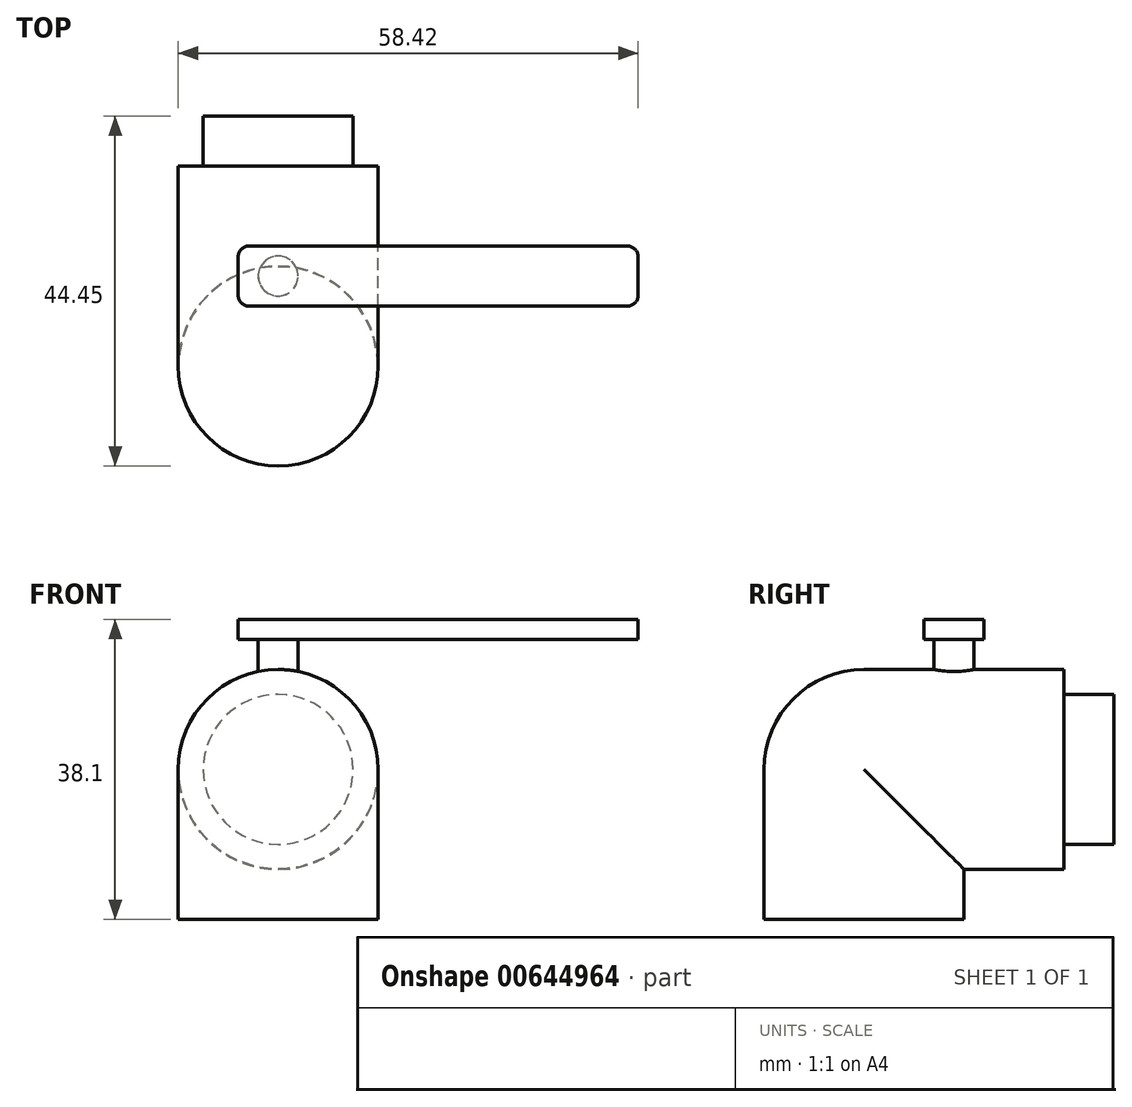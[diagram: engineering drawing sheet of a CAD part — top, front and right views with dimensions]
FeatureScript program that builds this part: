
annotation { "Feature Type Name" : "Feature", "Feature Type Description" : "" }
export const myFeature = defineFeature(function(context is Context, id is Id, definition is map)
    precondition{}
    {
        {
            var Q0;
            Q0=qCreatedBy(makeId("Front.planeOp"),FACE);
            var sketch = newSketch(context, id + "F0", { "sketchPlane" : qUnion([Q0])});
            skCircle(sketch, "E0", {"center": v(0, 0) * mm, "radius": 9.53 * mm});
            skSolve(sketch);
        }
        {
            var Q0;
            Q0 = qSketchRegion(id + "F0", true);
            extrude(context, id + "F1", {"entities" : qUnion([Q0]), "depth" : 6.35 * mm, "offsetDistance" : 25.4 * mm});
        }
        {
            var Q0;
            Q0=makeQuery(id+"F1.opExtrude","CAP_FACE",FACE,{"disambiguationData":[OSD([sQuery(id+"F0.wireOp",EDGE,"E0")])],"isStart":false});
            var sketch = newSketch(context, id + "F2", { "sketchPlane" : qUnion([Q0])});
            skCircle(sketch, "E1", {"center": v(0, 0) * mm, "radius": 12.7 * mm});
            skSolve(sketch);
        }
        {
            var Q0;
            Q0 = qSketchRegion(id + "F2", true);
            extrude(context, id + "F3", {"entities" : qUnion([Q0]), "operationType" : NewBodyOperationType.ADD, "depth" : 25.4 * mm, "offsetDistance" : 25.4 * mm});
        }
        {
            var Q0;
            Q0=qCreatedBy(makeId("Right.planeOp"),FACE);
            var sketch = newSketch(context, id + "F4", { "sketchPlane" : qUnion([Q0])});
            skLineSegment(sketch, "E2", {"start": v(-31.75, 0) * mm, "end": v(-31.75, 0) * mm});
            skArc(sketch, "E3", {"start": v(-31.75, 12.7) * mm, "mid": v(-40.73, 8.98) * mm, "end": v(-44.45, 0) * mm});
            skLineSegment(sketch, "E4", {"start": v(-44.45, 0) * mm, "end": v(-31.75, 0) * mm});
            skLineSegment(sketch, "E5", {"start": v(-31.75, 0) * mm, "end": v(-31.75, 12.7) * mm});
            skSolve(sketch);
        }
        {
            var Q0;
            Q0=makeQuery(id+"F4.imprint","IMPRINT",FACE,{"disambiguationData":[TD([[makeQuery(id+"F4.imprint","IMPRINT",EDGE,{"derivedFrom":sQuery(id+"F4.wireOp",EDGE,"E3")}),1.0]])]});
            var Q1;
            Q1=sQuery(id+"F4.wireOp",EDGE,"E5");
            revolve(context, id + "F5", {"operationType" : NewBodyOperationType.ADD, "entities" : qUnion([Q0]), "axis" : qUnion([Q1]), "revolveType" : RevolveType.FULL});
        }
        {
            var Q0;
            Q0=makeQuery(id+"F5.opRevolve","SWEPT_FACE",FACE,{"disambiguationData":[OSD([sQuery(id+"F4.wireOp",EDGE,"E4")])]});
            var sketch = newSketch(context, id + "F6", { "sketchPlane" : qUnion([Q0])});
            skCircle(sketch, "E6", {"center": v(0, 31.75) * mm, "radius": 12.7 * mm});
            skSolve(sketch);
        }
        {
            var Q0;
            Q0 = qSketchRegion(id + "F6", true);
            extrude(context, id + "F7", {"entities" : qUnion([Q0]), "operationType" : NewBodyOperationType.ADD, "depth" : 19.05 * mm, "offsetDistance" : 25.4 * mm});
        }
        {
            var Q0;
            Q0=qCreatedBy(makeId("Top.planeOp"),FACE);
            var sketch = newSketch(context, id + "F8", { "sketchPlane" : qUnion([Q0])});
            skCircle(sketch, "E7", {"center": v(0, -20.32) * mm, "radius": 2.54 * mm});
            skSolve(sketch);
        }
        {
            var Q0;
            Q0 = qSketchRegion(id + "F8", true);
            extrude(context, id + "F9", {"entities" : qUnion([Q0]), "operationType" : NewBodyOperationType.ADD, "depth" : 19.05 * mm, "offsetDistance" : 25.4 * mm});
        }
        {
            var Q0;
            Q0=makeQuery(id+"F9.opExtrude","CAP_FACE",FACE,{"disambiguationData":[OSD([sQuery(id+"F8.wireOp",EDGE,"E7")])],"isStart":false});
            var sketch = newSketch(context, id + "F10", { "sketchPlane" : qUnion([Q0])});
            skCircle(sketch, "E8", {"center": v(0, -20.32) * mm, "radius": 2.54 * mm});
            skLineSegment(sketch, "E9.bottom", {"start": v(44.36, -16.51) * mm, "end": v(-3.72, -16.51) * mm});
            skLineSegment(sketch, "E9.top", {"start": v(44.36, -24.13) * mm, "end": v(-3.72, -24.13) * mm});
            skLineSegment(sketch, "E9.left", {"start": v(45.72, -17.87) * mm, "end": v(45.72, -22.77) * mm});
            skLineSegment(sketch, "E9.right", {"start": v(-5.08, -17.87) * mm, "end": v(-5.08, -22.77) * mm});
            skPoint(sketch, "E10.visualSharp", {"position": v(-5.08, -16.51) * mm});
            skArc(sketch, "E10.filletArc", {"start": v(-3.72, -16.51) * mm, "mid": v(-4.68, -16.9) * mm, "end": v(-5.08, -17.87) * mm});
            skPoint(sketch, "E11.visualSharp", {"position": v(-5.08, -24.13) * mm});
            skArc(sketch, "E11.filletArc", {"start": v(-5.08, -22.77) * mm, "mid": v(-4.68, -23.73) * mm, "end": v(-3.72, -24.13) * mm});
            skPoint(sketch, "E12.visualSharp", {"position": v(45.72, -24.13) * mm});
            skArc(sketch, "E12.filletArc", {"start": v(44.36, -24.13) * mm, "mid": v(45.32, -23.73) * mm, "end": v(45.72, -22.77) * mm});
            skPoint(sketch, "E13.visualSharp", {"position": v(45.72, -16.5) * mm});
            skArc(sketch, "E13.filletArc", {"start": v(45.72, -17.87) * mm, "mid": v(45.32, -16.9) * mm, "end": v(44.36, -16.51) * mm});
            skSolve(sketch);
        }
        {
            var Q0;
            Q0=makeQuery(id+"F10.imprint","IMPRINT",FACE,{"disambiguationData":[TD([[makeQuery(id+"F10.imprint","IMPRINT",EDGE,{"derivedFrom":sQuery(id+"F10.wireOp",EDGE,"E8")}),-1.0]])]});
            extrude(context, id + "F11", {"entities" : qUnion([Q0]), "operationType" : NewBodyOperationType.ADD, "oppositeDirection" : true, "depth" : 2.54 * mm, "offsetDistance" : 25.4 * mm});
        }
    });
